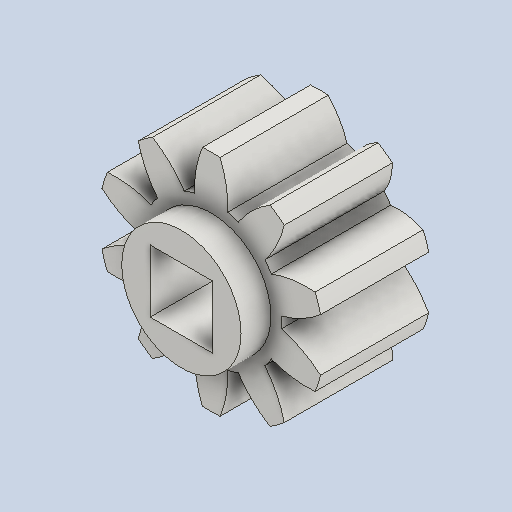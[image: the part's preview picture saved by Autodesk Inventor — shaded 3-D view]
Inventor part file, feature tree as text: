
AUTODESK INVENTOR PART (.ipt)
format: ipt  version: 2022 (Build 260153000, 153)  size: 290,304 bytes
history: native  units: in
note: dims shown in document units (in); Inventor stores cm internally (conversion verified against a paired STEP export)
features: other x12, sketch x6, plane x3
ambient origin geometry x8: Origin, YZ Plane, XZ Plane, XY Plane, X Axis, Y Axis, Z Axis, Center Point
bodies: Solid1 (feature_tree)
feature tree (21):
  other  "Spur Gear1"
  other  "Solid1::Spur Gear1"
  other  "TaggingFeature1"
  sketch  "Sketch1"  dims[d0=0.3937in]
  sketch  "Sketch2"  dims[d9=0.0in]
  sketch  "Sketch3"  dims[d14=0.0in]
  sketch  "Sketch4"  dims[d15=0.9352in]
  sketch  "Sketch5"  dims[d16=0.0in]
  sketch  "Sketch6"  dims[d17=0.0in d18=0.0in d19=0.9352in]
  plane  "XZ Plane_1"
  plane  "Work Plane2"
  plane  "Work Plane3"
  other  "Srf1"
  other  "Srf1::Derived"
  other  "Start plane iMate"
  other  "Distance iMate"
  other  "Position iMate"
  other  "Mesh iMate"
  other  "Axis iMate"
  other  "Mesh iMate2"
  other  "Align iMate"
